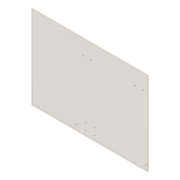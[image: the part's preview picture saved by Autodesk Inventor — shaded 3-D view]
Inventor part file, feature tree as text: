
AUTODESK INVENTOR PART (.ipt)
format: ipt  version: 2012 (Build 160160000, 160)  size: 99,328 bytes
history: native  units: in
note: dims shown in document units (in); Inventor stores cm internally (conversion verified against a paired STEP export)
features: hole x5, pattern_linear x3, extrude x1, sketch x1
ambient origin geometry x8: Origin, YZ Plane, XZ Plane, XY Plane, X Axis, Y Axis, Z Axis, Center Point
bodies: Solid1 (feature_tree)
feature tree (10):
  extrude  "Extrusion1"  Depth=31.5in
  hole  "Hole1"  [1 undecoded]
  pattern_linear  "Rectangular Pattern1"  Count1=2 Spacing1=2.625in
  hole  "Hole2"  [1 undecoded]
  pattern_linear  "Rectangular Pattern2"  Count1=2 Spacing1=3.0in
  hole  "Hole3"  [1 undecoded]
  pattern_linear  "Rectangular Pattern3"  [2 undecoded]
  hole  "Hole4"  [1 undecoded]
  hole  "Hole5"  [1 undecoded]
  sketch  "Sketch1"  dims[d0=44.0in d1=31.5in d2=0.5in d3=0.0in d4=20.4063in d5=1.625in d6=0.265in d7=0.75in d8=0.375in d9=0.25in d10=0.5635in d11=1.0in d12=0.8108in d13=0.7874in d15=2.625in d16=0.7874in d18=3.1875in d19=19.375in d20=5.625in d21=0.265in d22=0.75in d23=0.5in d24=0.25in d25=0.5635in d26=1.0in d27=0.8108in d28=0.7874in d30=3.0in d31=1.875in d32=5.625in d33=0.265in d34=0.75in d35=0.5in d36=0.25in d37=0.5635in d38=1.0in d39=0.8108in d40=0.7874in d42=3.0in d43=1.875in d44=16.75in d45=0.265in d46=0.75in d47=0.5in d48=0.25in d49=0.5635in d50=1.0in d51=0.8108in d52=0.625in d53=1.875in d54=0.265in d55=0.75in d56=0.5in d57=0.25in d58=0.5635in d59=1.0in d60=0.8108in]
note: 7 required parameter values undecoded (feature->parameter linkage not recoverable at this tier; creation-order binding heuristic only, values carry confidence <= 0.55)
